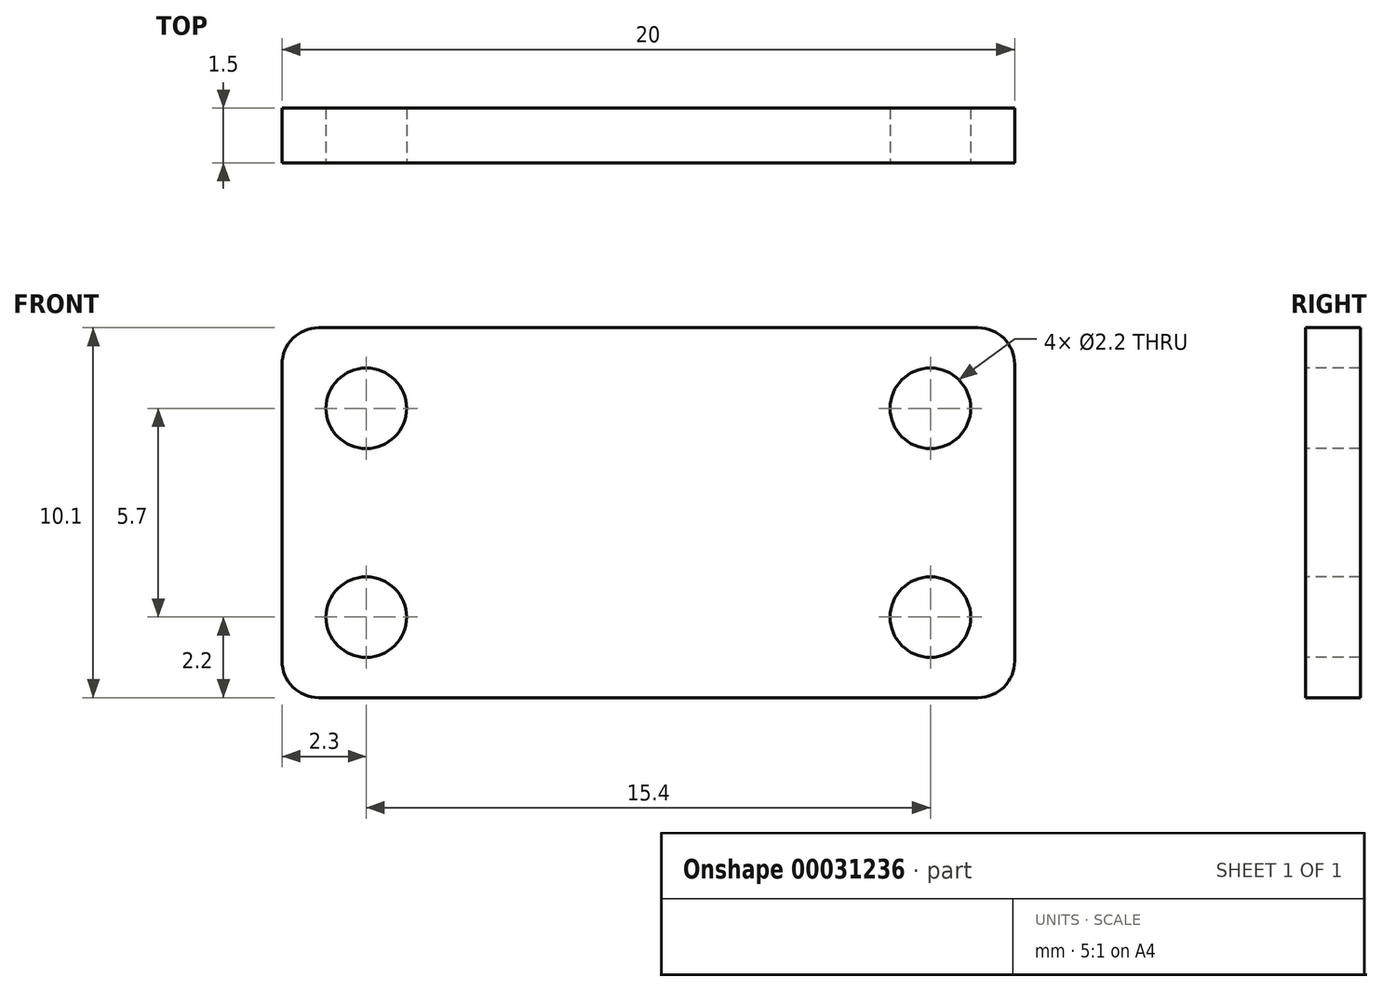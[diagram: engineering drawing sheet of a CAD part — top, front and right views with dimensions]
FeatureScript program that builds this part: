
annotation { "Feature Type Name" : "Feature", "Feature Type Description" : "" }
export const myFeature = defineFeature(function(context is Context, id is Id, definition is map)
    precondition{}
    {
        {
            var Q0;
            Q0=qCreatedBy(makeId("Front.planeOp"),FACE);
            var sketch = newSketch(context, id + "F0", { "sketchPlane" : qUnion([Q0])});
            skLineSegment(sketch, "E0.bottom", {"start": v(0, 0) * mm, "end": v(20, 0) * mm});
            skLineSegment(sketch, "E0.top", {"start": v(0, 10.1) * mm, "end": v(20, 10.1) * mm});
            skLineSegment(sketch, "E0.left", {"start": v(0, 0) * mm, "end": v(0, 10.1) * mm});
            skLineSegment(sketch, "E0.right", {"start": v(20, 0) * mm, "end": v(20, 10.1) * mm});
            skSolve(sketch);
        }
        {
            var Q0;
            Q0 = qSketchRegion(id + "F0", true);
            extrude(context, id + "F1", {"entities" : qUnion([Q0]), "depth" : 1.5 * mm});
        }
        {
            var Q0;
            Q0=makeQuery(id+"F1.opExtrude","CAP_FACE",FACE,{"disambiguationData":[OSD([sQuery(id+"F0.wireOp",EDGE,"E0.bottom"),sQuery(id+"F0.wireOp",EDGE,"E0.top"),sQuery(id+"F0.wireOp",EDGE,"E0.left"),sQuery(id+"F0.wireOp",EDGE,"E0.right")])],"isStart":false});
            var sketch = newSketch(context, id + "F2", { "sketchPlane" : qUnion([Q0])});
            skLineSegment(sketch, "E1", {"start": v(0, 5.05) * mm, "end": v(20, 5.05) * mm, "construction": true});
            skLineSegment(sketch, "E2", {"start": v(10, 10.1) * mm, "end": v(10, 0) * mm, "construction": true});
            skPoint(sketch, "E3", {"position": v(10, 5.05) * mm});
            skCircle(sketch, "E4", {"center": v(2.3, 7.9) * mm, "radius": 1.1 * mm});
            skCircle(sketch, "E5.MirrorC", {"center": v(17.7, 7.9) * mm, "radius": 1.1 * mm});
            skCircle(sketch, "E6.MirrorC", {"center": v(2.3, 2.2) * mm, "radius": 1.1 * mm});
            skCircle(sketch, "E7.MirrorC", {"center": v(17.7, 2.2) * mm, "radius": 1.1 * mm});
            skSolve(sketch);
        }
        {
            var Q0;
            Q0 = qSketchRegion(id + "F2", true);
            extrude(context, id + "F3", {"entities" : qUnion([Q0]), "operationType" : NewBodyOperationType.REMOVE, "endBound" : BoundingType.UP_TO_NEXT, "oppositeDirection" : true, "depth" : 25 * mm});
        }
        {
            var Q0;
            Q0=makeQuery(id+"F1.opExtrude","SWEPT_EDGE",EDGE,{"disambiguationData":[OSD([sQuery(id+"F0.wireOp",EDGE,"E0.top"),sQuery(id+"F0.wireOp",EDGE,"E0.right")])]});
            var Q1;
            Q1=makeQuery(id+"F1.opExtrude","SWEPT_EDGE",EDGE,{"disambiguationData":[OSD([sQuery(id+"F0.wireOp",EDGE,"E0.bottom"),sQuery(id+"F0.wireOp",EDGE,"E0.right")])]});
            var Q2;
            Q2=makeQuery(id+"F1.opExtrude","SWEPT_EDGE",EDGE,{"disambiguationData":[OSD([sQuery(id+"F0.wireOp",EDGE,"E0.top"),sQuery(id+"F0.wireOp",EDGE,"E0.left")])]});
            var Q3;
            Q3=makeQuery(id+"F1.opExtrude","SWEPT_EDGE",EDGE,{"disambiguationData":[OSD([sQuery(id+"F0.wireOp",EDGE,"E0.bottom"),sQuery(id+"F0.wireOp",EDGE,"E0.left")])]});
            fillet(context, id + "F4", {"entities" : qUnion([Q0, Q1, Q2, Q3]), "radius" : 1 * mm, "tangentPropagation" : true, "allowEdgeOverflow" : false});
        }
    });
